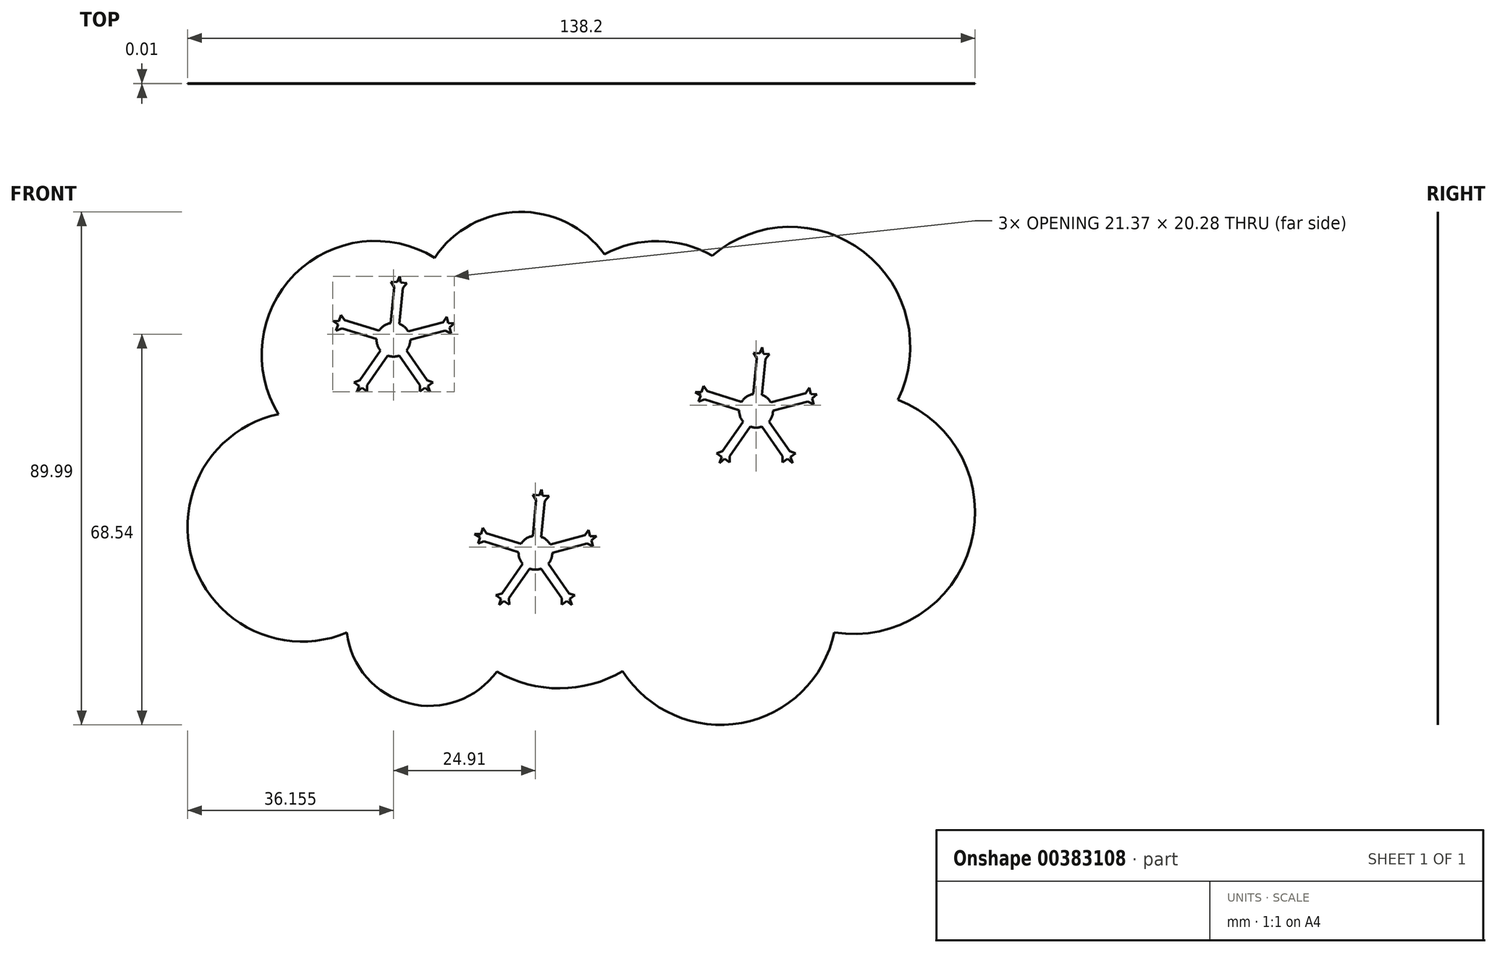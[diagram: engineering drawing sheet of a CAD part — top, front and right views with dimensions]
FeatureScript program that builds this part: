
annotation { "Feature Type Name" : "Feature", "Feature Type Description" : "" }
export const myFeature = defineFeature(function(context is Context, id is Id, definition is map)
    precondition{}
    {
        {
            var Q0;
            Q0=qCreatedBy(makeId("Front.planeOp"),FACE);
            var sketch = newSketch(context, id + "F0", { "sketchPlane" : qUnion([Q0])});
            skArc(sketch, "E0", {"start": v(-5.21, 27.72) * mm, "mid": v(-29.74, 24.82) * mm, "end": v(-32.63, 0.28) * mm});
            skArc(sketch, "E1", {"start": v(24.58, 28.35) * mm, "mid": v(9.52, 35.75) * mm, "end": v(-5.21, 27.72) * mm});
            skArc(sketch, "E2", {"start": v(43.53, 28.1) * mm, "mid": v(34.09, 30.63) * mm, "end": v(24.58, 28.35) * mm});
            skArc(sketch, "E3", {"start": v(64.92, -38) * mm, "mid": v(88.87, -22.62) * mm, "end": v(76.1, 2.83) * mm});
            skArc(sketch, "E4", {"start": v(27.78, -44.8) * mm, "mid": v(48.63, -53.9) * mm, "end": v(64.92, -38) * mm});
            skArc(sketch, "E5", {"start": v(5.7, -44.86) * mm, "mid": v(16.75, -47.82) * mm, "end": v(27.78, -44.8) * mm});
            skArc(sketch, "E6", {"start": v(-20.63, -38.05) * mm, "mid": v(-9.78, -50.43) * mm, "end": v(5.7, -44.86) * mm});
            skArc(sketch, "E7", {"start": v(-32.63, 0.28) * mm, "mid": v(-47.66, -25.47) * mm, "end": v(-20.63, -38.05) * mm});
            skArc(sketch, "E8.trimOffspring", {"start": v(76.1, 2.83) * mm, "mid": v(70.1, 28.71) * mm, "end": v(43.53, 28.1) * mm});
            skLineSegment(sketch, "E9", {"start": v(-12.92, 16.26) * mm, "end": v(-12.32, 22.56) * mm});
            skLineSegment(sketch, "E10", {"start": v(-11.4, 16.11) * mm, "end": v(-10.8, 22.41) * mm});
            skLineSegment(sketch, "E11", {"start": v(-9.86, 14.8) * mm, "end": v(-3.74, 16.4) * mm});
            skLineSegment(sketch, "E12", {"start": v(-9.47, 13.32) * mm, "end": v(-3.35, 14.93) * mm});
            skLineSegment(sketch, "E13", {"start": v(-15.4, 13.45) * mm, "end": v(-21.45, 15.31) * mm});
            skLineSegment(sketch, "E14", {"start": v(-14.95, 14.9) * mm, "end": v(-21, 16.77) * mm});
            skLineSegment(sketch, "E15", {"start": v(-14.7, 11.42) * mm, "end": v(-18.32, 6.23) * mm});
            skLineSegment(sketch, "E16", {"start": v(-13.45, 10.54) * mm, "end": v(-17.07, 5.35) * mm});
            skLineSegment(sketch, "E17", {"start": v(-11.42, 10.54) * mm, "end": v(-7.8, 5.35) * mm});
            skLineSegment(sketch, "E18", {"start": v(-10.17, 11.42) * mm, "end": v(-6.55, 6.23) * mm});
            skArc(sketch, "E19.trimOffspring", {"start": v(-9.86, 14.8) * mm, "mid": v(-10.52, 15.6) * mm, "end": v(-11.4, 16.11) * mm});
            skArc(sketch, "E20.trimOffspring", {"start": v(-10.17, 11.42) * mm, "mid": v(-9.65, 12.3) * mm, "end": v(-9.47, 13.32) * mm});
            skArc(sketch, "E21.trimOffspring", {"start": v(-13.45, 10.54) * mm, "mid": v(-12.44, 10.36) * mm, "end": v(-11.42, 10.54) * mm});
            skArc(sketch, "E22.trimOffspring", {"start": v(-15.4, 13.45) * mm, "mid": v(-15.24, 12.37) * mm, "end": v(-14.7, 11.42) * mm});
            skArc(sketch, "E23.trimOffspring", {"start": v(-12.92, 16.26) * mm, "mid": v(-14.08, 15.8) * mm, "end": v(-14.95, 14.9) * mm});
            skLineSegment(sketch, "E24", {"start": v(-12.32, 22.56) * mm, "end": v(-10.8, 22.41) * mm});
            skLineSegment(sketch, "E25", {"start": v(-3.74, 16.4) * mm, "end": v(-3.12, 17.33) * mm});
            skLineSegment(sketch, "E26", {"start": v(-3.12, 17.33) * mm, "end": v(-2.85, 16.25) * mm});
            skLineSegment(sketch, "E27", {"start": v(-2.85, 16.25) * mm, "end": v(-1.74, 16.22) * mm});
            skLineSegment(sketch, "E28", {"start": v(-1.74, 16.22) * mm, "end": v(-2.62, 15.53) * mm});
            skLineSegment(sketch, "E29", {"start": v(-2.62, 15.53) * mm, "end": v(-2.35, 14.45) * mm});
            skLineSegment(sketch, "E30", {"start": v(-2.35, 14.45) * mm, "end": v(-3.35, 14.93) * mm});
            skLineSegment(sketch, "E31", {"start": v(-12.32, 22.56) * mm, "end": v(-12.88, 23.52) * mm});
            skLineSegment(sketch, "E32", {"start": v(-12.88, 23.52) * mm, "end": v(-11.77, 23.41) * mm});
            skLineSegment(sketch, "E33", {"start": v(-11.77, 23.41) * mm, "end": v(-11.37, 24.45) * mm});
            skLineSegment(sketch, "E34", {"start": v(-11.37, 24.45) * mm, "end": v(-11.17, 23.35) * mm});
            skLineSegment(sketch, "E35", {"start": v(-11.17, 23.35) * mm, "end": v(-10.06, 23.25) * mm});
            skLineSegment(sketch, "E36", {"start": v(-10.06, 23.25) * mm, "end": v(-10.8, 22.41) * mm});
            skLineSegment(sketch, "E37", {"start": v(-7.8, 5.35) * mm, "end": v(-6.55, 6.23) * mm});
            skLineSegment(sketch, "E38", {"start": v(-6.55, 6.23) * mm, "end": v(-5.5, 5.86) * mm});
            skLineSegment(sketch, "E39", {"start": v(-5.5, 5.86) * mm, "end": v(-6.41, 5.22) * mm});
            skLineSegment(sketch, "E40", {"start": v(-6.41, 5.22) * mm, "end": v(-6.05, 4.17) * mm});
            skLineSegment(sketch, "E41", {"start": v(-6.05, 4.17) * mm, "end": v(-6.91, 4.88) * mm});
            skLineSegment(sketch, "E42", {"start": v(-6.91, 4.88) * mm, "end": v(-7.82, 4.24) * mm});
            skLineSegment(sketch, "E43", {"start": v(-7.82, 4.24) * mm, "end": v(-7.8, 5.35) * mm});
            skLineSegment(sketch, "E44", {"start": v(-3.74, 16.4) * mm, "end": v(-3.35, 14.93) * mm});
            skLineSegment(sketch, "E45", {"start": v(-21, 16.77) * mm, "end": v(-21.45, 15.31) * mm});
            skLineSegment(sketch, "E46", {"start": v(-18.32, 6.23) * mm, "end": v(-17.07, 5.35) * mm});
            skLineSegment(sketch, "E47", {"start": v(-21, 16.77) * mm, "end": v(-21.67, 17.66) * mm});
            skLineSegment(sketch, "E48", {"start": v(-21.67, 17.66) * mm, "end": v(-22, 16.6) * mm});
            skLineSegment(sketch, "E49", {"start": v(-22, 16.6) * mm, "end": v(-23.11, 16.62) * mm});
            skLineSegment(sketch, "E50", {"start": v(-23.11, 16.62) * mm, "end": v(-22.18, 16.01) * mm});
            skLineSegment(sketch, "E51", {"start": v(-22.18, 16.01) * mm, "end": v(-22.5, 14.95) * mm});
            skLineSegment(sketch, "E52", {"start": v(-22.5, 14.95) * mm, "end": v(-21.45, 15.31) * mm});
            skLineSegment(sketch, "E53", {"start": v(-18.32, 6.23) * mm, "end": v(-19.38, 5.86) * mm});
            skLineSegment(sketch, "E54", {"start": v(-19.38, 5.86) * mm, "end": v(-18.46, 5.22) * mm});
            skLineSegment(sketch, "E55", {"start": v(-18.46, 5.22) * mm, "end": v(-18.83, 4.17) * mm});
            skLineSegment(sketch, "E56", {"start": v(-18.83, 4.17) * mm, "end": v(-17.97, 4.88) * mm});
            skLineSegment(sketch, "E57", {"start": v(-17.97, 4.88) * mm, "end": v(-17.05, 4.24) * mm});
            skLineSegment(sketch, "E58", {"start": v(-17.05, 4.24) * mm, "end": v(-17.07, 5.35) * mm});
            skLineSegment(sketch, "E59", {"start": v(50.7, 3.8) * mm, "end": v(51.31, 10.1) * mm});
            skLineSegment(sketch, "E60", {"start": v(52.22, 3.66) * mm, "end": v(52.83, 9.96) * mm});
            skLineSegment(sketch, "E61", {"start": v(53.77, 2.34) * mm, "end": v(59.9, 3.95) * mm});
            skLineSegment(sketch, "E62", {"start": v(54.16, 0.87) * mm, "end": v(60.28, 2.47) * mm});
            skLineSegment(sketch, "E63", {"start": v(48.23, 1) * mm, "end": v(42.18, 2.86) * mm});
            skLineSegment(sketch, "E64", {"start": v(48.67, 2.45) * mm, "end": v(42.63, 4.31) * mm});
            skLineSegment(sketch, "E65", {"start": v(48.92, -1.04) * mm, "end": v(45.3, -6.23) * mm});
            skLineSegment(sketch, "E66", {"start": v(50.17, -1.91) * mm, "end": v(46.55, -7.1) * mm});
            skLineSegment(sketch, "E67", {"start": v(52.2, -1.91) * mm, "end": v(55.83, -7.1) * mm});
            skLineSegment(sketch, "E68", {"start": v(53.46, -1.04) * mm, "end": v(57.08, -6.23) * mm});
            skArc(sketch, "E69.trimOffspring", {"start": v(53.77, 2.34) * mm, "mid": v(53.11, 3.14) * mm, "end": v(52.22, 3.66) * mm});
            skArc(sketch, "E70.trimOffspring", {"start": v(53.46, -1.04) * mm, "mid": v(53.98, -0.15) * mm, "end": v(54.16, 0.87) * mm});
            skArc(sketch, "E71.trimOffspring", {"start": v(50.17, -1.91) * mm, "mid": v(51.2, -2.1) * mm, "end": v(52.2, -1.91) * mm});
            skArc(sketch, "E72.trimOffspring", {"start": v(48.23, 1) * mm, "mid": v(48.38, -0.09) * mm, "end": v(48.92, -1.04) * mm});
            skArc(sketch, "E73.trimOffspring", {"start": v(50.7, 3.8) * mm, "mid": v(49.54, 3.35) * mm, "end": v(48.67, 2.45) * mm});
            skLineSegment(sketch, "E74", {"start": v(51.31, 10.1) * mm, "end": v(52.83, 9.96) * mm});
            skLineSegment(sketch, "E75", {"start": v(59.9, 3.95) * mm, "end": v(60.5, 4.88) * mm});
            skLineSegment(sketch, "E76", {"start": v(60.5, 4.88) * mm, "end": v(60.78, 3.8) * mm});
            skLineSegment(sketch, "E77", {"start": v(60.78, 3.8) * mm, "end": v(61.89, 3.76) * mm});
            skLineSegment(sketch, "E78", {"start": v(61.89, 3.76) * mm, "end": v(61.01, 3.07) * mm});
            skLineSegment(sketch, "E79", {"start": v(61.01, 3.07) * mm, "end": v(61.28, 2) * mm});
            skLineSegment(sketch, "E80", {"start": v(61.28, 2) * mm, "end": v(60.28, 2.47) * mm});
            skLineSegment(sketch, "E81", {"start": v(51.31, 10.1) * mm, "end": v(50.75, 11.06) * mm});
            skLineSegment(sketch, "E82", {"start": v(50.75, 11.06) * mm, "end": v(51.85, 10.96) * mm});
            skLineSegment(sketch, "E83", {"start": v(51.85, 10.96) * mm, "end": v(52.26, 12) * mm});
            skLineSegment(sketch, "E84", {"start": v(52.26, 12) * mm, "end": v(52.46, 10.9) * mm});
            skLineSegment(sketch, "E85", {"start": v(52.46, 10.9) * mm, "end": v(53.57, 10.8) * mm});
            skLineSegment(sketch, "E86", {"start": v(53.57, 10.8) * mm, "end": v(52.83, 9.96) * mm});
            skLineSegment(sketch, "E87", {"start": v(55.83, -7.1) * mm, "end": v(57.08, -6.23) * mm});
            skLineSegment(sketch, "E88", {"start": v(57.08, -6.23) * mm, "end": v(58.13, -6.6) * mm});
            skLineSegment(sketch, "E89", {"start": v(58.13, -6.6) * mm, "end": v(57.22, -7.23) * mm});
            skLineSegment(sketch, "E90", {"start": v(57.22, -7.23) * mm, "end": v(57.58, -8.28) * mm});
            skLineSegment(sketch, "E91", {"start": v(57.58, -8.28) * mm, "end": v(56.72, -7.58) * mm});
            skLineSegment(sketch, "E92", {"start": v(56.72, -7.58) * mm, "end": v(55.8, -8.21) * mm});
            skLineSegment(sketch, "E93", {"start": v(55.8, -8.21) * mm, "end": v(55.83, -7.1) * mm});
            skLineSegment(sketch, "E94", {"start": v(59.9, 3.95) * mm, "end": v(60.28, 2.47) * mm});
            skLineSegment(sketch, "E95", {"start": v(42.63, 4.31) * mm, "end": v(42.18, 2.86) * mm});
            skLineSegment(sketch, "E96", {"start": v(45.3, -6.23) * mm, "end": v(46.55, -7.1) * mm});
            skLineSegment(sketch, "E97", {"start": v(42.63, 4.31) * mm, "end": v(41.96, 5.2) * mm});
            skLineSegment(sketch, "E98", {"start": v(41.96, 5.2) * mm, "end": v(41.63, 4.14) * mm});
            skLineSegment(sketch, "E99", {"start": v(41.63, 4.14) * mm, "end": v(40.52, 4.16) * mm});
            skLineSegment(sketch, "E100", {"start": v(40.52, 4.16) * mm, "end": v(41.45, 3.56) * mm});
            skLineSegment(sketch, "E101", {"start": v(41.45, 3.56) * mm, "end": v(41.12, 2.5) * mm});
            skLineSegment(sketch, "E102", {"start": v(41.12, 2.5) * mm, "end": v(42.18, 2.86) * mm});
            skLineSegment(sketch, "E103", {"start": v(45.3, -6.23) * mm, "end": v(44.25, -6.6) * mm});
            skLineSegment(sketch, "E104", {"start": v(44.25, -6.6) * mm, "end": v(45.17, -7.23) * mm});
            skLineSegment(sketch, "E105", {"start": v(45.17, -7.23) * mm, "end": v(44.8, -8.28) * mm});
            skLineSegment(sketch, "E106", {"start": v(44.8, -8.28) * mm, "end": v(45.66, -7.58) * mm});
            skLineSegment(sketch, "E107", {"start": v(45.66, -7.58) * mm, "end": v(46.58, -8.21) * mm});
            skLineSegment(sketch, "E108", {"start": v(46.58, -8.21) * mm, "end": v(46.55, -7.1) * mm});
            skLineSegment(sketch, "E109", {"start": v(11.99, -21.1) * mm, "end": v(12.6, -14.8) * mm});
            skLineSegment(sketch, "E110", {"start": v(13.5, -21.25) * mm, "end": v(14.1, -14.95) * mm});
            skLineSegment(sketch, "E111", {"start": v(15.05, -22.57) * mm, "end": v(21.17, -20.96) * mm});
            skLineSegment(sketch, "E112", {"start": v(15.44, -24.04) * mm, "end": v(21.56, -22.44) * mm});
            skLineSegment(sketch, "E113", {"start": v(9.5, -23.92) * mm, "end": v(3.46, -22.05) * mm});
            skLineSegment(sketch, "E114", {"start": v(9.96, -22.46) * mm, "end": v(3.9, -20.6) * mm});
            skLineSegment(sketch, "E115", {"start": v(10.2, -25.95) * mm, "end": v(6.59, -31.14) * mm});
            skLineSegment(sketch, "E116", {"start": v(11.46, -26.82) * mm, "end": v(7.84, -32.01) * mm});
            skLineSegment(sketch, "E117", {"start": v(13.49, -26.82) * mm, "end": v(17.1, -32.01) * mm});
            skLineSegment(sketch, "E118", {"start": v(14.74, -25.95) * mm, "end": v(18.36, -31.14) * mm});
            skArc(sketch, "E119.trimOffspring", {"start": v(15.05, -22.57) * mm, "mid": v(14.4, -21.77) * mm, "end": v(13.5, -21.25) * mm});
            skArc(sketch, "E120.trimOffspring", {"start": v(14.74, -25.95) * mm, "mid": v(15.26, -25.06) * mm, "end": v(15.44, -24.04) * mm});
            skArc(sketch, "E121.trimOffspring", {"start": v(11.46, -26.82) * mm, "mid": v(12.47, -27) * mm, "end": v(13.49, -26.82) * mm});
            skArc(sketch, "E122.trimOffspring", {"start": v(9.5, -23.92) * mm, "mid": v(9.67, -25) * mm, "end": v(10.2, -25.95) * mm});
            skArc(sketch, "E123.trimOffspring", {"start": v(11.99, -21.1) * mm, "mid": v(10.83, -21.56) * mm, "end": v(9.96, -22.46) * mm});
            skLineSegment(sketch, "E124", {"start": v(12.6, -14.8) * mm, "end": v(14.1, -14.95) * mm});
            skLineSegment(sketch, "E125", {"start": v(21.17, -20.96) * mm, "end": v(21.79, -20.03) * mm});
            skLineSegment(sketch, "E126", {"start": v(21.79, -20.03) * mm, "end": v(22.06, -21.11) * mm});
            skLineSegment(sketch, "E127", {"start": v(22.06, -21.11) * mm, "end": v(23.17, -21.15) * mm});
            skLineSegment(sketch, "E128", {"start": v(23.17, -21.15) * mm, "end": v(22.3, -21.84) * mm});
            skLineSegment(sketch, "E129", {"start": v(22.3, -21.84) * mm, "end": v(22.56, -22.92) * mm});
            skLineSegment(sketch, "E130", {"start": v(22.56, -22.92) * mm, "end": v(21.56, -22.44) * mm});
            skLineSegment(sketch, "E131", {"start": v(12.6, -14.8) * mm, "end": v(12.03, -13.85) * mm});
            skLineSegment(sketch, "E132", {"start": v(12.03, -13.85) * mm, "end": v(13.14, -13.95) * mm});
            skLineSegment(sketch, "E133", {"start": v(13.14, -13.95) * mm, "end": v(13.54, -12.92) * mm});
            skLineSegment(sketch, "E134", {"start": v(13.54, -12.92) * mm, "end": v(13.74, -14.01) * mm});
            skLineSegment(sketch, "E135", {"start": v(13.74, -14.01) * mm, "end": v(14.85, -14.12) * mm});
            skLineSegment(sketch, "E136", {"start": v(14.85, -14.12) * mm, "end": v(14.1, -14.95) * mm});
            skLineSegment(sketch, "E137", {"start": v(17.1, -32.01) * mm, "end": v(18.36, -31.14) * mm});
            skLineSegment(sketch, "E138", {"start": v(18.36, -31.14) * mm, "end": v(19.41, -31.5) * mm});
            skLineSegment(sketch, "E139", {"start": v(19.41, -31.5) * mm, "end": v(18.5, -32.14) * mm});
            skLineSegment(sketch, "E140", {"start": v(18.5, -32.14) * mm, "end": v(18.86, -33.2) * mm});
            skLineSegment(sketch, "E141", {"start": v(18.86, -33.2) * mm, "end": v(18, -32.49) * mm});
            skLineSegment(sketch, "E142", {"start": v(18, -32.49) * mm, "end": v(17.09, -33.12) * mm});
            skLineSegment(sketch, "E143", {"start": v(17.09, -33.12) * mm, "end": v(17.1, -32.01) * mm});
            skLineSegment(sketch, "E144", {"start": v(21.17, -20.96) * mm, "end": v(21.56, -22.44) * mm});
            skLineSegment(sketch, "E145", {"start": v(3.9, -20.6) * mm, "end": v(3.46, -22.05) * mm});
            skLineSegment(sketch, "E146", {"start": v(6.59, -31.14) * mm, "end": v(7.84, -32.01) * mm});
            skLineSegment(sketch, "E147", {"start": v(3.9, -20.6) * mm, "end": v(3.24, -19.7) * mm});
            skLineSegment(sketch, "E148", {"start": v(3.24, -19.7) * mm, "end": v(2.91, -20.77) * mm});
            skLineSegment(sketch, "E149", {"start": v(2.91, -20.77) * mm, "end": v(1.8, -20.75) * mm});
            skLineSegment(sketch, "E150", {"start": v(1.8, -20.75) * mm, "end": v(2.73, -21.35) * mm});
            skLineSegment(sketch, "E151", {"start": v(2.73, -21.35) * mm, "end": v(2.4, -22.42) * mm});
            skLineSegment(sketch, "E152", {"start": v(2.4, -22.42) * mm, "end": v(3.46, -22.05) * mm});
            skLineSegment(sketch, "E153", {"start": v(6.59, -31.14) * mm, "end": v(5.53, -31.5) * mm});
            skLineSegment(sketch, "E154", {"start": v(5.53, -31.5) * mm, "end": v(6.45, -32.14) * mm});
            skLineSegment(sketch, "E155", {"start": v(6.45, -32.14) * mm, "end": v(6.08, -33.2) * mm});
            skLineSegment(sketch, "E156", {"start": v(6.08, -33.2) * mm, "end": v(6.94, -32.49) * mm});
            skLineSegment(sketch, "E157", {"start": v(6.94, -32.49) * mm, "end": v(7.86, -33.12) * mm});
            skLineSegment(sketch, "E158", {"start": v(7.86, -33.12) * mm, "end": v(7.84, -32.01) * mm});
            skSolve(sketch);
        }
        {
            var Q0;
            Q0=makeQuery(id+"F0.imprint","IMPRINT",FACE,{"disambiguationData":[TD([[makeQuery(id+"F0.imprint","IMPRINT",EDGE,{"derivedFrom":sQuery(id+"F0.wireOp",EDGE,"E0")}),1.0]])]});
            extrude(context, id + "F1", {"entities" : qUnion([Q0]), "depth" : 1 / 101.6 * mm});
        }
    });
